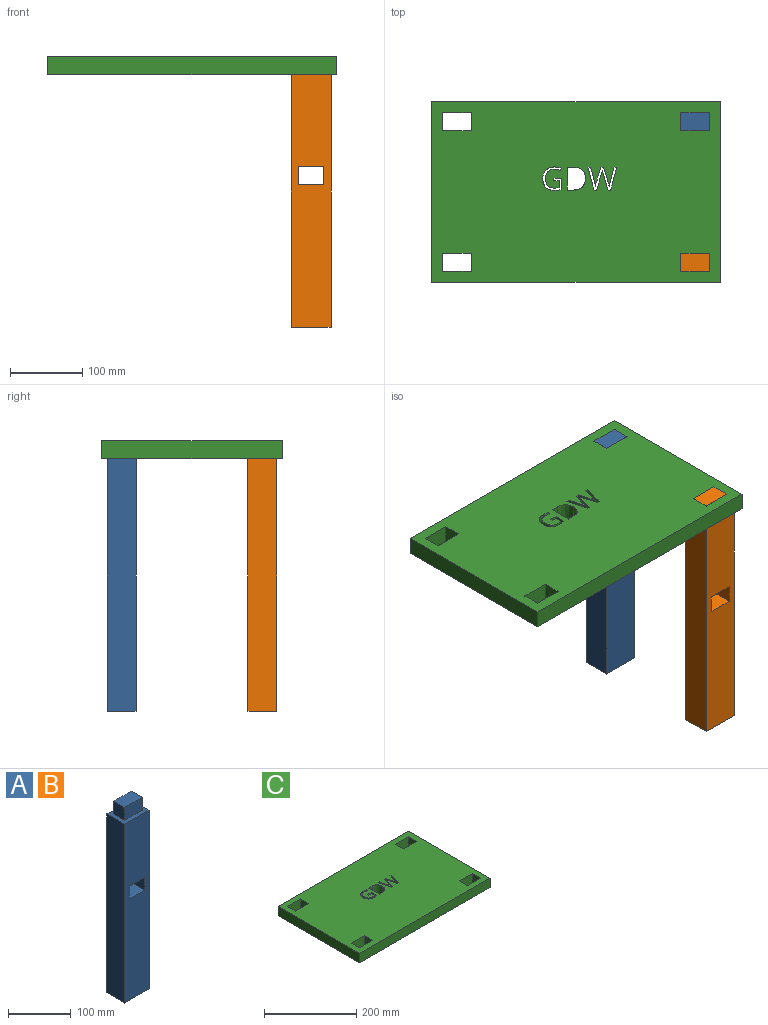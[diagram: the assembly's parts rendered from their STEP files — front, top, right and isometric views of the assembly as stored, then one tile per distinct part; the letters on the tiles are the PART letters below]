
ASSEMBLY  parts=3 mates=2
PART A: 15 faces, bbox 55x40x375 mm
  f0: plane 350x55mm, normal (0,1,0), area 18375mm2, adj f2,f3,f4,f5,f11,f12,f13,f14
  f1: plane 350x55mm, normal (0,-1,0), area 18375mm2, adj f2,f3,f4,f5,f11,f12,f13,f14
  f2: plane 55x40mm, normal (0,0,1), area 1202.8mm2, adj f0,f1,f3,f4,f6,f7,f8,f9
  f3: plane 350x40mm, normal (-1,0,0), area 14000mm2, adj f0,f1,f2,f5
  f4: plane 350x40mm, normal (1,0,0), area 14000mm2, adj f0,f1,f2,f5
  f5: plane 55x40mm, normal (0,0,-1), area 2200mm2, adj f0,f1,f3,f4
  f6: plane 40x25mm, normal (0,1,0), area 1000mm2, adj f2,f7,f9,f10
  f7: plane 25x24.93mm, normal (-1,0,0), area 623.3mm2, adj f2,f6,f8,f10
  f8: plane 40x25mm, normal (0,-1,0), area 1000mm2, adj f2,f7,f9,f10
  f9: plane 25x24.93mm, normal (1,0,0), area 623.3mm2, adj f2,f6,f8,f10
  f10: plane 40x24.93mm, normal (0,0,1), area 997.2mm2, adj f6,f7,f8,f9
  f11: plane 40x35mm, normal (0,0,-1), area 1400mm2, adj f0,f1,f12,f14
  f12: plane 40x25mm, normal (1,0,0), area 1000mm2, adj f0,f1,f11,f13
  f13: plane 40x35mm, normal (0,0,1), area 1400mm2, adj f0,f1,f12,f14
  f14: plane 40x25mm, normal (-1,0,0), area 1000mm2, adj f0,f1,f11,f13
PART B: same geometry as A
PART C: 69 faces, bbox 400x250x25 mm
  f0: plane 400x25mm, normal (0,1,0), area 10000mm2, adj f1,f66,f67,f68
  f1: plane 250x25mm, normal (-1,0,0), area 6250mm2, adj f0,f2,f67,f68
  f2: plane 400x25mm, normal (0,-1,0), area 10000mm2, adj f1,f66,f67,f68
  f3: plane 25x25mm, normal (1,0,0), area 625mm2, adj f4,f59,f67,f68
  f4: plane 40x25mm, normal (0,-1,0), area 1000mm2, adj f3,f5,f67,f68
  f5: plane 25x25mm, normal (-1,0,0), area 625mm2, adj f4,f59,f67,f68
  f6: plane 25x25mm, normal (1,0,0), area 625mm2, adj f7,f60,f67,f68
  f7: plane 40x25mm, normal (0,-1,0), area 1000mm2, adj f6,f8,f67,f68
  f8: plane 25x25mm, normal (-1,0,0), area 625mm2, adj f7,f60,f67,f68
  f9: plane 25x25mm, normal (1,0,0), area 625mm2, adj f10,f61,f67,f68
  f10: plane 40x25mm, normal (0,-1,0), area 1000mm2, adj f9,f11,f67,f68
  f11: plane 25x25mm, normal (-1,0,0), area 625mm2, adj f10,f61,f67,f68
  f12: plane 25x25mm, normal (1,0,0), area 625mm2, adj f13,f62,f67,f68
  f13: plane 40x25mm, normal (0,-1,0), area 1000mm2, adj f12,f14,f67,f68
  f14: plane 25x25mm, normal (-1,0,0), area 625mm2, adj f13,f62,f67,f68
  f15: plane 31.73x25mm, normal (-0.97,0.26,0), area 821.2mm2, adj f16,f63,f67,f68
  f16: plane 25x3.65mm, normal (0,1,0), area 91.2mm2, adj f15,f17,f67,f68
  f17: plane 25x21.25mm, normal (0.96,0.29,0), area 554.7mm2, adj f16,f18,f67,f68
  f18: extruded ~25x3.56mm, area 92.7mm2, adj f17,f19,f67,f68
  f19: extruded ~25x2.58mm, area 66.3mm2, adj f18,f20,f67,f68
  f20: extruded ~25x6.27mm, area 161.4mm2, adj f19,f21,f67,f68
  f21: plane 25x21.12mm, normal (-0.96,0.28,0), area 550.3mm2, adj f20,f22,f67,f68
  f22: plane 25x3.65mm, normal (0,1,0), area 91.2mm2, adj f21,f23,f67,f68
  f23: plane 31.73x25mm, normal (0.97,0.26,0), area 820.9mm2, adj f22,f24,f67,f68
  f24: plane 25x3.91mm, normal (0,-1,0), area 97.8mm2, adj f23,f25,f67,f68
  f25: plane 25x19.6mm, normal (-0.97,-0.25,0), area 505.8mm2, adj f24,f26,f67,f68
  f26: extruded ~25x7.47mm, area 190.6mm2, adj f25,f27,f67,f68
  f27: extruded ~25x7.77mm, area 199.3mm2, adj f26,f28,f67,f68
  f28: plane 25x19.29mm, normal (0.96,-0.28,0), area 502.8mm2, adj f27,f29,f67,f68
  f29: plane 25x3.91mm, normal (0,-1,0), area 97.8mm2, adj f28,f30,f67,f68
  f30: plane 25x19.47mm, normal (-0.96,-0.29,0), area 509mm2, adj f29,f31,f67,f68
  f31: extruded ~25x7.6mm, area 195.1mm2, adj f30,f32,f67,f68
  f32: extruded ~25x7.51mm, area 191.8mm2, adj f31,f33,f67,f68
  f33: plane 25x19.56mm, normal (0.97,-0.25,0), area 504.6mm2, adj f32,f63,f67,f68
  f34: extruded ~25x11.46mm, area 312.7mm2, adj f35,f64,f67,f68
  f35: extruded ~25x12.01mm, area 327.6mm2, adj f34,f36,f67,f68
  f36: extruded ~25x12.27mm, area 332.3mm2, adj f35,f37,f67,f68
  f37: plane 25x8.79mm, normal (0,1,0), area 219.8mm2, adj f36,f38,f67,f68
  f38: plane 31.73x25mm, normal (1,0,0), area 793.3mm2, adj f37,f39,f67,f68
  f39: plane 25x9.72mm, normal (0,-1,0), area 243.1mm2, adj f38,f64,f67,f68
  f40: plane 25x3.3mm, normal (1,0,0), area 82.5mm2, adj f41,f65,f67,f68
  f41: plane 25x10.79mm, normal (0,-1,0), area 269.6mm2, adj f40,f42,f67,f68
  f42: plane 25x15.43mm, normal (-1,0,0), area 385.8mm2, adj f41,f43,f67,f68
  f43: extruded ~25x5.13mm, area 131.8mm2, adj f42,f44,f67,f68
  f44: extruded ~25x6.04mm, area 151.4mm2, adj f43,f45,f67,f68
  f45: extruded ~25x11.22mm, area 309.2mm2, adj f44,f46,f67,f68
  f46: extruded ~25x12.01mm, area 324.4mm2, adj f45,f47,f67,f68
  f47: extruded ~25x8.67mm, area 224.8mm2, adj f46,f48,f67,f68
  f48: extruded ~25x5.72mm, area 204.7mm2, adj f47,f49,f67,f68
  f49: extruded ~25x8.74mm, area 226.2mm2, adj f48,f50,f67,f68
  f50: extruded ~25x9.47mm, area 242.8mm2, adj f49,f51,f67,f68
  f51: plane 25x3.26mm, normal (-0.92,0.4,0), area 88.9mm2, adj f50,f52,f67,f68
  f52: extruded ~25x8.27mm, area 213.2mm2, adj f51,f53,f67,f68
  f53: extruded ~25x9.05mm, area 249.3mm2, adj f52,f54,f67,f68
  f54: extruded ~25x9.57mm, area 259.2mm2, adj f53,f55,f67,f68
  f55: extruded ~25x9.74mm, area 262.2mm2, adj f54,f56,f67,f68
  f56: extruded ~25x9.21mm, area 252mm2, adj f55,f57,f67,f68
  f57: extruded ~25x6.45mm, area 162.6mm2, adj f56,f58,f67,f68
  f58: plane 25x9.77mm, normal (1,0,0), area 244.1mm2, adj f57,f65,f67,f68
  f59: plane 40x25mm, normal (0,1,0), area 1000mm2, adj f3,f5,f67,f68
  f60: plane 40x25mm, normal (0,1,0), area 1000mm2, adj f6,f8,f67,f68
  f61: plane 40x25mm, normal (0,1,0), area 1000mm2, adj f9,f11,f67,f68
  f62: plane 40x25mm, normal (0,1,0), area 1000mm2, adj f12,f14,f67,f68
  f63: plane 25x3.91mm, normal (0,-1,0), area 97.8mm2, adj f15,f33,f67,f68
  f64: extruded ~25x11.5mm, area 313.7mm2, adj f34,f39,f67,f68
  f65: plane 25x7.09mm, normal (0,1,0), area 177.3mm2, adj f40,f58,f67,f68
  f66: plane 250x25mm, normal (1,0,0), area 6250mm2, adj f0,f2,f67,f68
  f67: plane 400x250mm, normal (0,0,1), area 94552.3mm2, adj f0,f1,f2,f3,f4,f5,f6,f7
  f68: plane 400x250mm, normal (0,0,-1), area 94552.3mm2, adj f0,f1,f2,f3,f4,f5,f6,f7
PLACE A t=(26.56,145,-279.67)mm
PLACE B t=(26.56,-50,-279.67)mm
PLACE C t=(-332.76,-63.17,70.33)mm
MATE fastened C.f67 <-> B.f10  axis (0,0,1) through (-1.35,-38.17,95.33)mm
MATE fastened A.f10 <-> C.f67  axis (0,0,1) through (-1.35,156.83,95.33)mm
